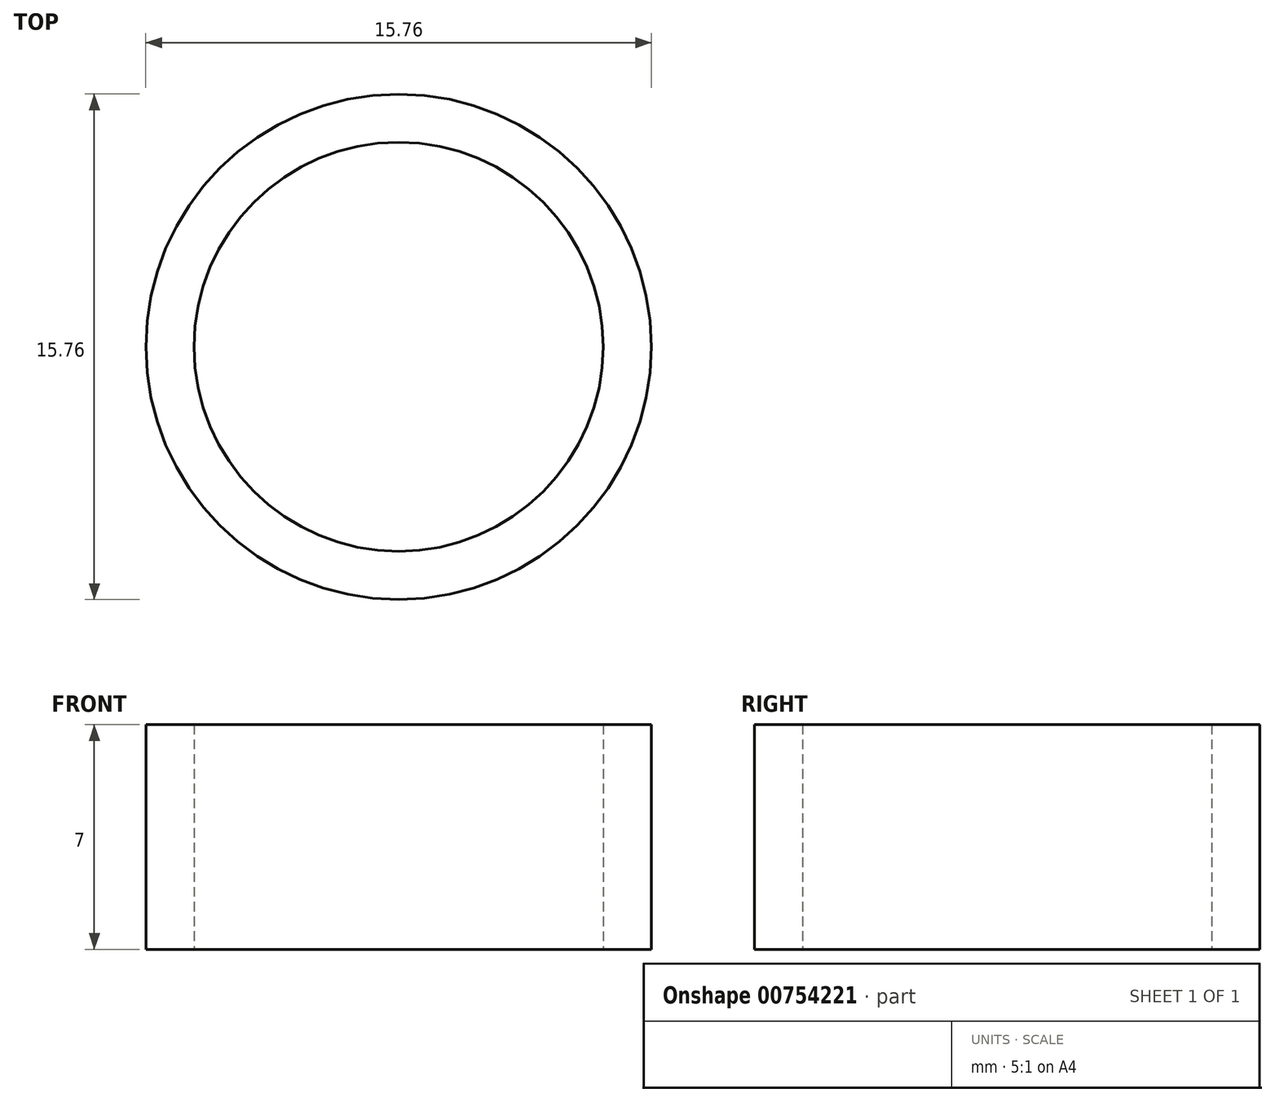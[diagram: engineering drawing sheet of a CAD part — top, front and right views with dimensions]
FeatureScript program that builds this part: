
annotation { "Feature Type Name" : "Feature", "Feature Type Description" : "" }
export const myFeature = defineFeature(function(context is Context, id is Id, definition is map)
    precondition{}
    {
        {
            var Q0;
            Q0=qCreatedBy(makeId("Top.planeOp"),FACE);
            var sketch = newSketch(context, id + "F0", { "sketchPlane" : qUnion([Q0])});
            skCircle(sketch, "E0", {"center": v(0, 0) * mm, "radius": 7.88 * mm});
            skCircle(sketch, "E1.0", {"center": v(0, 0) * mm, "radius": 6.38 * mm});
            skSolve(sketch);
        }
        {
            var Q0;
            Q0 = qSketchRegion(id + "F0", true);
            extrude(context, id + "F1", {"entities" : qUnion([Q0]), "depth" : 7 * mm, "offsetDistance" : 25 * mm});
        }
    });
